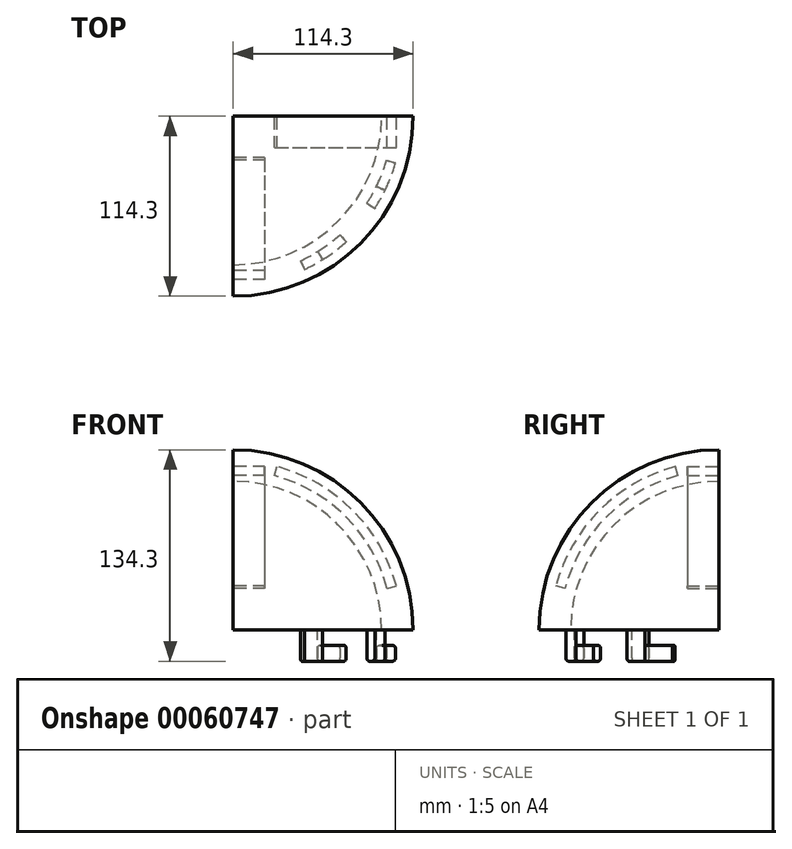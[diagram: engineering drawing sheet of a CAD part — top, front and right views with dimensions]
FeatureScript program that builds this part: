
annotation { "Feature Type Name" : "Feature", "Feature Type Description" : "" }
export const myFeature = defineFeature(function(context is Context, id is Id, definition is map)
    precondition{}
    {
        {
            var Q0;
            Q0=qCreatedBy(makeId("Right.planeOp"),FACE);
            var sketch = newSketch(context, id + "F0", { "sketchPlane" : qUnion([Q0])});
            skArc(sketch, "E0", {"start": v(0, 114.3) * mm, "mid": v(-80.82, 80.82) * mm, "end": v(-114.3, 0) * mm});
            skArc(sketch, "E1", {"start": v(0, 94.3) * mm, "mid": v(-66.68, 66.68) * mm, "end": v(-94.3, 0) * mm});
            skLineSegment(sketch, "E2", {"start": v(0, 94.3) * mm, "end": v(0, 114.3) * mm});
            skLineSegment(sketch, "E3", {"start": v(-94.3, 0) * mm, "end": v(-114.3, 0) * mm});
            skSolve(sketch);
        }
        {
            var Q0;
            Q0=makeQuery(id+"F0.imprint","IMPRINT",FACE,{"disambiguationData":[TD([[makeQuery(id+"F0.imprint","IMPRINT",EDGE,{"derivedFrom":sQuery(id+"F0.wireOp",EDGE,"E0")}),1.0]])]});
            var Q1;
            Q1=sQuery(id+"F0.wireOp",EDGE,"E2");
            revolve(context, id + "F1", {"entities" : qUnion([Q0]), "axis" : qUnion([Q1]), "revolveType" : RevolveType.ONE_DIRECTION, "angle" : 90 * degree});
        }
        {
            var Q0;
            Q0=makeQuery(id+"F1.opRevolve","CAP_FACE",FACE,{"disambiguationData":[OSD([sQuery(id+"F0.wireOp",EDGE,"E0"),sQuery(id+"F0.wireOp",EDGE,"E1"),sQuery(id+"F0.wireOp",EDGE,"E2"),sQuery(id+"F0.wireOp",EDGE,"E3")])],"isStart":false});
            var sketch = newSketch(context, id + "F2", { "sketchPlane" : qUnion([Q0])});
            skArc(sketch, "E4", {"start": v(-27.77, 103.64) * mm, "mid": v(-75.87, 75.87) * mm, "end": v(-103.64, 27.77) * mm});
            skArc(sketch, "E5", {"start": v(-26.22, 97.85) * mm, "mid": v(-71.63, 71.63) * mm, "end": v(-97.85, 26.22) * mm});
            skLineSegment(sketch, "E6", {"start": v(0, 0) * mm, "end": v(-27.77, 103.64) * mm});
            skLineSegment(sketch, "E7", {"start": v(-97.85, 26.22) * mm, "end": v(-103.64, 27.77) * mm});
            skSolve(sketch);
        }
        {
            var Q0;
            Q0=makeQuery(id+"F2.imprint","IMPRINT",FACE,{"disambiguationData":[TD([[makeQuery(id+"F2.imprint","IMPRINT",EDGE,{"derivedFrom":sQuery(id+"F2.wireOp",EDGE,"E4")}),1.0]])]});
            extrude(context, id + "F3", {"entities" : qUnion([Q0]), "operationType" : NewBodyOperationType.REMOVE, "oppositeDirection" : true, "depth" : 20 * mm});
        }
        {
            var Q0;
            Q0=makeQuery(id+"F0.imprint","IMPRINT",FACE,{"disambiguationData":[TD([[makeQuery(id+"F0.imprint","IMPRINT",EDGE,{"derivedFrom":sQuery(id+"F0.wireOp",EDGE,"E0")}),1.0]])]});
            var sketch = newSketch(context, id + "F4", { "sketchPlane" : qUnion([Q0])});
            skArc(sketch, "E8.0", {"start": v(-26.22, 97.85) * mm, "mid": v(-71.63, 71.63) * mm, "end": v(-97.85, 26.22) * mm});
            skArc(sketch, "E9.0", {"start": v(-27.77, 103.64) * mm, "mid": v(-75.87, 75.87) * mm, "end": v(-103.64, 27.77) * mm});
            skLineSegment(sketch, "E10", {"start": v(-26.22, 97.85) * mm, "end": v(-27.77, 103.64) * mm});
            skLineSegment(sketch, "E11", {"start": v(-97.85, 26.22) * mm, "end": v(-103.64, 27.77) * mm});
            skSolve(sketch);
        }
        {
            var Q0;
            Q0=makeQuery(id+"F4.imprint","IMPRINT",FACE,{"disambiguationData":[TD([[makeQuery(id+"F4.imprint","IMPRINT",EDGE,{"derivedFrom":sQuery(id+"F4.wireOp",EDGE,"E8.0")}),-1.0]])]});
            extrude(context, id + "F5", {"entities" : qUnion([Q0]), "operationType" : NewBodyOperationType.REMOVE, "depth" : 20 * mm});
        }
        {
            var Q0;
            Q0=makeQuery(id+"F5.boolean.opBoolean","MERGE",FACE,{"derivedFrom":[makeQuery(id+"F3.boolean.opBoolean","MERGE",FACE,{"derivedFrom":[makeQuery(id+"F1.opRevolve","SWEPT_FACE",FACE,{"disambiguationData":[OSD([sQuery(id+"F0.wireOp",EDGE,"E3")])]}),makeQuery(id+"F3.opExtrude","SWEPT_FACE",FACE,{"disambiguationData":[OSD([sQuery(id+"F2.wireOp",EDGE,"tj54Cu89-9J1S-AJKw-QeEM-ljXHSpR1f2pj")])]})]}),makeQuery(id+"F5.opExtrude","SWEPT_FACE",FACE,{"disambiguationData":[OSD([sQuery(id+"F4.wireOp",EDGE,"EMUQLBOC-9Rso-lLbz-JRUg-i4oPmn0DbPj1")])]})]});
            var sketch = newSketch(context, id + "F6", { "sketchPlane" : qUnion([Q0])});
            skArc(sketch, "E12", {"start": v(91.05, 44.4) * mm, "mid": v(88.17, 49.88) * mm, "end": v(84.96, 55.17) * mm});
            skArc(sketch, "E13", {"start": v(96.44, 47.04) * mm, "mid": v(93.39, 52.84) * mm, "end": v(89.99, 58.44) * mm});
            skLineSegment(sketch, "E14", {"start": v(42.81, 91.8) * mm, "end": v(45.35, 97.25) * mm});
            skLineSegment(sketch, "E15", {"start": v(53.68, 85.9) * mm, "end": v(56.86, 91) * mm});
            skLineSegment(sketch, "E16", {"start": v(84.96, 55.17) * mm, "end": v(89.99, 58.44) * mm});
            skLineSegment(sketch, "E17", {"start": v(91.05, 44.4) * mm, "end": v(96.44, 47.04) * mm});
            skArc(sketch, "E18.trimOffspring", {"start": v(53.68, 85.9) * mm, "mid": v(48.34, 89.02) * mm, "end": v(42.81, 91.8) * mm});
            skArc(sketch, "E19.trimOffspring", {"start": v(56.86, 91) * mm, "mid": v(51.2, 94.3) * mm, "end": v(45.35, 97.25) * mm});
            skSolve(sketch);
        }
        {
            var Q0;
            Q0=makeQuery(id+"F6.imprint","IMPRINT",FACE,{"disambiguationData":[TD([[makeQuery(id+"F6.imprint","IMPRINT",EDGE,{"derivedFrom":sQuery(id+"F6.wireOp",EDGE,"E14")}),-1.0]])]});
            var Q1;
            Q1=makeQuery(id+"F6.imprint","IMPRINT",FACE,{"disambiguationData":[TD([[makeQuery(id+"F6.imprint","IMPRINT",EDGE,{"derivedFrom":sQuery(id+"F6.wireOp",EDGE,"E12")}),-1.0]])]});
            extrude(context, id + "F7", {"entities" : qUnion([Q0, Q1]), "operationType" : NewBodyOperationType.ADD, "depth" : 20 * mm});
        }
        {
            var Q0;
            Q0=makeQuery(id+"F7.opExtrude","CAP_FACE",FACE,{"disambiguationData":[OSD([sQuery(id+"F6.wireOp",EDGE,"E14"),sQuery(id+"F6.wireOp",EDGE,"E15"),sQuery(id+"F6.wireOp",EDGE,"E18.trimOffspring"),sQuery(id+"F6.wireOp",EDGE,"E19.trimOffspring")])],"isStart":false});
            var sketch = newSketch(context, id + "F8", { "sketchPlane" : qUnion([Q0])});
            skArc(sketch, "E20", {"start": v(67.78, 75.28) * mm, "mid": v(60.96, 80.9) * mm, "end": v(53.68, 85.9) * mm});
            skArc(sketch, "E21", {"start": v(71.8, 79.74) * mm, "mid": v(64.57, 85.7) * mm, "end": v(56.86, 91) * mm});
            skLineSegment(sketch, "E22", {"start": v(53.68, 85.9) * mm, "end": v(56.86, 91) * mm});
            skLineSegment(sketch, "E23", {"start": v(67.78, 75.28) * mm, "end": v(71.8, 79.74) * mm});
            skSolve(sketch);
        }
        {
            var Q0;
            Q0=makeQuery(id+"F8.imprint","IMPRINT",FACE,{"disambiguationData":[TD([[makeQuery(id+"F8.imprint","IMPRINT",EDGE,{"derivedFrom":sQuery(id+"F8.wireOp",EDGE,"E20")}),-1.0]])]});
            extrude(context, id + "F9", {"entities" : qUnion([Q0]), "oppositeDirection" : true, "depth" : 10 * mm});
        }
        {
            var Q0;
            Q0=makeQuery(id+"F7.opExtrude","CAP_FACE",FACE,{"disambiguationData":[OSD([sQuery(id+"F6.wireOp",EDGE,"E12"),sQuery(id+"F6.wireOp",EDGE,"E13"),sQuery(id+"F6.wireOp",EDGE,"E16"),sQuery(id+"F6.wireOp",EDGE,"E17")])],"isStart":false});
            var sketch = newSketch(context, id + "F10", { "sketchPlane" : qUnion([Q0])});
            skArc(sketch, "E24", {"start": v(97.38, 27.92) * mm, "mid": v(94.57, 36.3) * mm, "end": v(91.05, 44.4) * mm});
            skArc(sketch, "E25", {"start": v(103.14, 29.58) * mm, "mid": v(100.17, 38.45) * mm, "end": v(96.44, 47.04) * mm});
            skLineSegment(sketch, "E26", {"start": v(91.05, 44.4) * mm, "end": v(96.44, 47.04) * mm});
            skLineSegment(sketch, "E27", {"start": v(97.38, 27.92) * mm, "end": v(103.14, 29.58) * mm});
            skSolve(sketch);
        }
        {
            var Q0;
            Q0=makeQuery(id+"F10.imprint","IMPRINT",FACE,{"disambiguationData":[TD([[makeQuery(id+"F10.imprint","IMPRINT",EDGE,{"derivedFrom":sQuery(id+"F10.wireOp",EDGE,"E24")}),-1.0]])]});
            extrude(context, id + "F11", {"entities" : qUnion([Q0]), "oppositeDirection" : true, "depth" : 10 * mm});
        }
        {
            var Q0;
            Q0=makeQuery(id+"F7.opExtrude","CAP_EDGE",EDGE,{"disambiguationData":[OSD([sQuery(id+"F6.wireOp",EDGE,"E19.trimOffspring")])],"isStart":false});
            var Q1;
            Q1=makeQuery(id+"F7.opExtrude","CAP_EDGE",EDGE,{"disambiguationData":[OSD([sQuery(id+"F6.wireOp",EDGE,"E18.trimOffspring")])],"isStart":false});
            var Q2;
            Q2=makeQuery(id+"F9.opExtrude","CAP_EDGE",EDGE,{"disambiguationData":[OSD([sQuery(id+"F8.wireOp",EDGE,"E20")])],"isStart":true});
            var Q3;
            Q3=makeQuery(id+"F9.opExtrude","CAP_EDGE",EDGE,{"disambiguationData":[OSD([sQuery(id+"F8.wireOp",EDGE,"E21")])],"isStart":true});
            var Q4;
            Q4=makeQuery(id+"F7.opExtrude","CAP_EDGE",EDGE,{"disambiguationData":[OSD([sQuery(id+"F6.wireOp",EDGE,"E12")])],"isStart":false});
            var Q5;
            Q5=makeQuery(id+"F11.opExtrude","CAP_EDGE",EDGE,{"disambiguationData":[OSD([sQuery(id+"F10.wireOp",EDGE,"E24")])],"isStart":true});
            var Q6;
            Q6=makeQuery(id+"F11.opExtrude","CAP_EDGE",EDGE,{"disambiguationData":[OSD([sQuery(id+"F10.wireOp",EDGE,"E25")])],"isStart":true});
            var Q7;
            Q7=makeQuery(id+"F7.opExtrude","CAP_EDGE",EDGE,{"disambiguationData":[OSD([sQuery(id+"F6.wireOp",EDGE,"E13")])],"isStart":false});
            var Q8;
            Q8=makeQuery(id+"F9.opExtrude","CAP_EDGE",EDGE,{"disambiguationData":[OSD([sQuery(id+"F8.wireOp",EDGE,"E21")])],"isStart":false});
            var Q9;
            Q9=makeQuery(id+"F9.opExtrude","CAP_EDGE",EDGE,{"disambiguationData":[OSD([sQuery(id+"F8.wireOp",EDGE,"E20")])],"isStart":false});
            var Q10;
            Q10=makeQuery(id+"F11.opExtrude","CAP_EDGE",EDGE,{"disambiguationData":[OSD([sQuery(id+"F10.wireOp",EDGE,"E25")])],"isStart":false});
            var Q11;
            Q11=makeQuery(id+"F11.opExtrude","CAP_EDGE",EDGE,{"disambiguationData":[OSD([sQuery(id+"F10.wireOp",EDGE,"E24")])],"isStart":false});
            fillet(context, id + "F12", {"entities" : qUnion([Q0, Q1, Q2, Q3, Q4, Q5, Q6, Q7, Q8, Q9, Q10, Q11]), "radius" : 2 * mm, "tangentPropagation" : true, "allowEdgeOverflow" : false});
        }
    });
